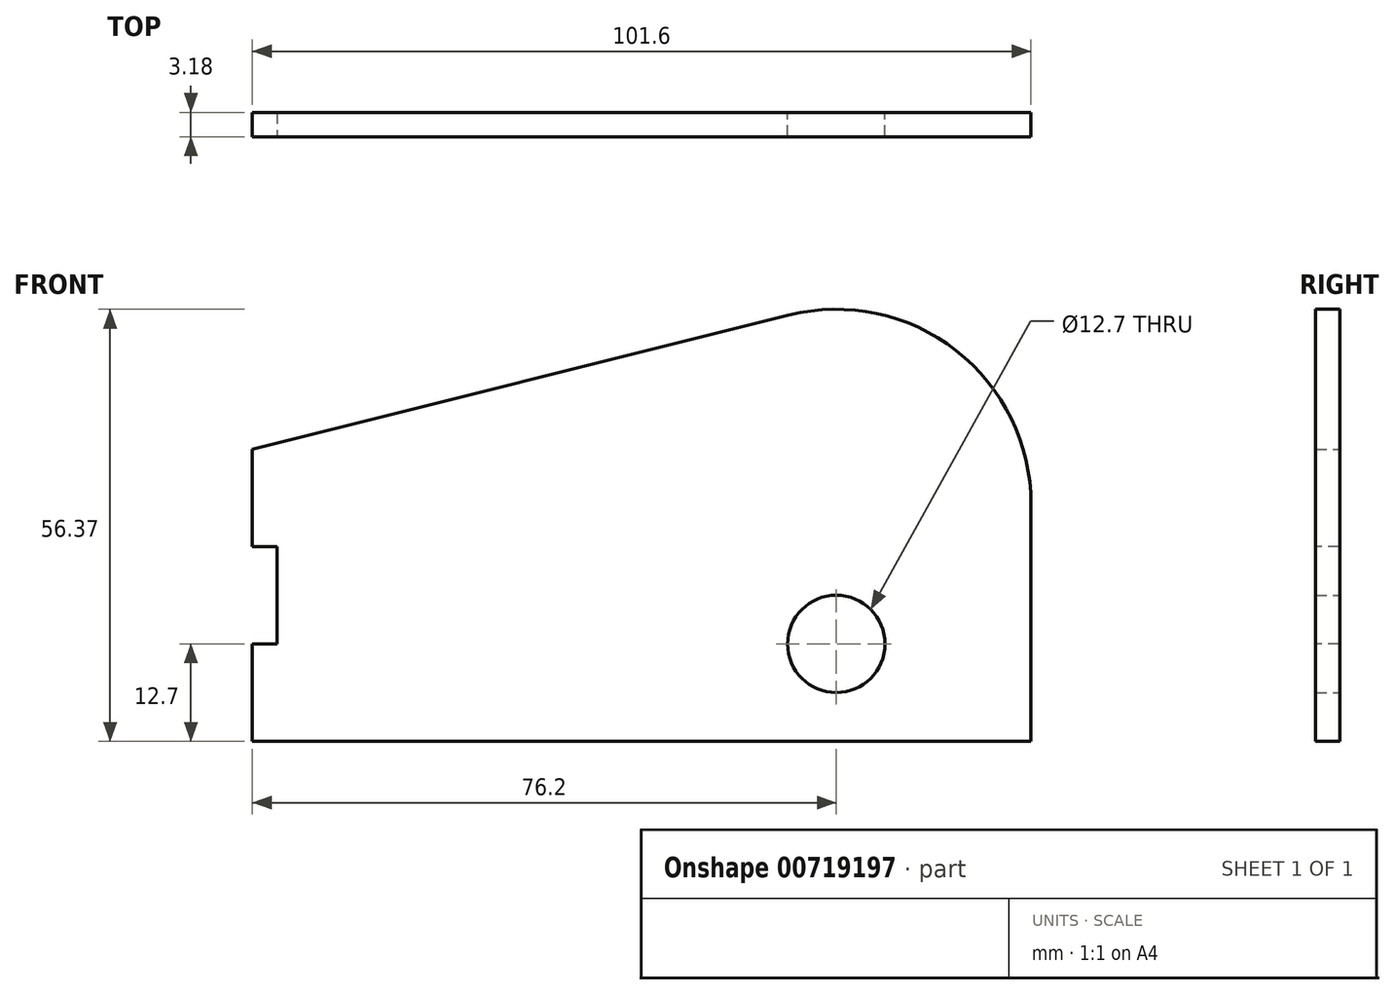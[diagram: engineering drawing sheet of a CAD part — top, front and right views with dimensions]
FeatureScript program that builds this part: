
annotation { "Feature Type Name" : "Feature", "Feature Type Description" : "" }
export const myFeature = defineFeature(function(context is Context, id is Id, definition is map)
    precondition{}
    {
        {
            var Q0;
            Q0=qCreatedBy(makeId("Front.planeOp"),FACE);
            var sketch = newSketch(context, id + "F0", { "sketchPlane" : qUnion([Q0])});
            skLineSegment(sketch, "E0", {"start": v(0, 0) * mm, "end": v(101.6, 0) * mm});
            skLineSegment(sketch, "E1", {"start": v(101.6, 0) * mm, "end": v(101.6, 30.97) * mm});
            skLineSegment(sketch, "E2", {"start": v(70.04, 55.6) * mm, "end": v(0, 38.1) * mm});
            skLineSegment(sketch, "E3", {"start": v(0, 38.1) * mm, "end": v(0, 0) * mm});
            skCircle(sketch, "E4", {"center": v(76.2, 12.7) * mm, "radius": 6.35 * mm});
            skPoint(sketch, "E5.visualSharp", {"position": v(101.6, 63.5) * mm});
            skArc(sketch, "E5.filletArc", {"start": v(101.6, 30.97) * mm, "mid": v(91.83, 50.99) * mm, "end": v(70.04, 55.6) * mm});
            skSolve(sketch);
        }
        {
            var Q0;
            Q0=makeQuery(id+"F0.imprint","IMPRINT",FACE,{"disambiguationData":[TD([[makeQuery(id+"F0.imprint","IMPRINT",EDGE,{"derivedFrom":sQuery(id+"F0.wireOp",EDGE,"E0")}),1.0]])]});
            extrude(context, id + "F1", {"entities" : qUnion([Q0]), "depth" : 3.17 * mm, "offsetDistance" : 25.4 * mm});
        }
        {
            var Q0;
            Q0=makeQuery(id+"F1.opExtrude","CAP_FACE",FACE,{"disambiguationData":[OSD([sQuery(id+"F0.wireOp",EDGE,"E0"),sQuery(id+"F0.wireOp",EDGE,"E1"),sQuery(id+"F0.wireOp",EDGE,"E2"),sQuery(id+"F0.wireOp",EDGE,"E3"),sQuery(id+"F0.wireOp",EDGE,"E4"),sQuery(id+"F0.wireOp",EDGE,"E5.filletArc")])],"isStart":false});
            var sketch = newSketch(context, id + "F2", { "sketchPlane" : qUnion([Q0])});
            skLineSegment(sketch, "E6.bottom", {"start": v(0, 25.4) * mm, "end": v(3.23, 25.4) * mm});
            skLineSegment(sketch, "E6.top", {"start": v(0, 12.7) * mm, "end": v(3.23, 12.7) * mm});
            skLineSegment(sketch, "E6.left", {"start": v(0, 25.4) * mm, "end": v(0, 12.7) * mm});
            skLineSegment(sketch, "E6.right", {"start": v(3.23, 25.4) * mm, "end": v(3.23, 12.7) * mm});
            skLineSegment(sketch, "E7", {"start": v(0, 38.1) * mm, "end": v(0, 25.4) * mm, "construction": true});
            skLineSegment(sketch, "E8", {"start": v(0, 12.7) * mm, "end": v(0, 0) * mm, "construction": true});
            skSolve(sketch);
        }
        {
            var Q0;
            Q0=makeQuery(id+"F2.imprint","IMPRINT",FACE,{"disambiguationData":[TD([[makeQuery(id+"F2.imprint","IMPRINT",EDGE,{"derivedFrom":sQuery(id+"F2.wireOp",EDGE,"E6.bottom")}),-1.0]])]});
            extrude(context, id + "F3", {"entities" : qUnion([Q0]), "operationType" : NewBodyOperationType.REMOVE, "oppositeDirection" : true, "depth" : 3.17 * mm, "offsetDistance" : 25.4 * mm});
        }
    });
